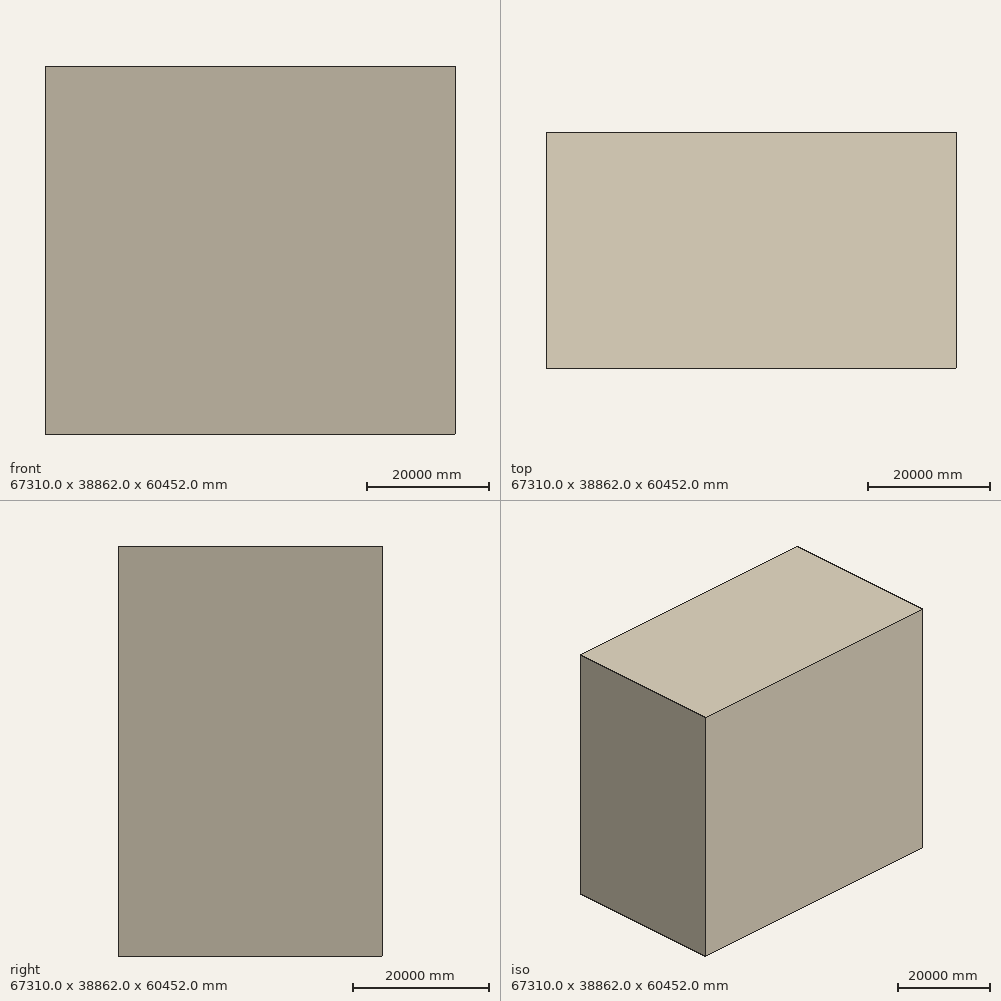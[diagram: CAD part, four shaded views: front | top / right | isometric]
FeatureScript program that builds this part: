
annotation { "Feature Type Name" : "Feature", "Feature Type Description" : "" }
export const myFeature = defineFeature(function(context is Context, id is Id, definition is map)
    precondition{}
    {
        {
            var Q0;
            Q0=qCreatedBy(makeId("Front.planeOp"),FACE);
            var sketch = newSketch(context, id + "F0", { "sketchPlane" : qUnion([Q0])});
            skLineSegment(sketch, "E0.bottom", {"start": v(33655, 30226) * mm, "end": v(-33655, 30226) * mm});
            skLineSegment(sketch, "E0.top", {"start": v(33655, -30226) * mm, "end": v(-33655, -30226) * mm});
            skLineSegment(sketch, "E0.left", {"start": v(33655, 30226) * mm, "end": v(33655, -30226) * mm});
            skLineSegment(sketch, "E0.right", {"start": v(-33655, 30226) * mm, "end": v(-33655, -30226) * mm});
            skPoint(sketch, "E0.middle", {"position": v(0, 0) * mm});
            skSolve(sketch);
        }
        {
            var Q0;
            Q0 = qSketchRegion(id + "F0", true);
            extrude(context, id + "F1", {"entities" : qUnion([Q0]), "depth" : 19431 * mm});
        }
        {
            var Q0;
            Q0=makeQuery(id+"F1.opExtrude","CAP_FACE",FACE,{"disambiguationData":[OSD([sQuery(id+"F0.wireOp",EDGE,"E0.bottom"),sQuery(id+"F0.wireOp",EDGE,"E0.top"),sQuery(id+"F0.wireOp",EDGE,"E0.left"),sQuery(id+"F0.wireOp",EDGE,"E0.right")])],"isStart":true});
            var sketch = newSketch(context, id + "F2", { "sketchPlane" : qUnion([Q0])});
            skLineSegment(sketch, "E1", {"start": v(20955, -30226) * mm, "end": v(20955, -4064) * mm});
            skLineSegment(sketch, "E2", {"start": v(20955, -4064) * mm, "end": v(6985, -4064) * mm});
            skLineSegment(sketch, "E3", {"start": v(6985, -4064) * mm, "end": v(6985, 17526) * mm});
            skLineSegment(sketch, "E4", {"start": v(6985, 17526) * mm, "end": v(-20955, 17526) * mm});
            skLineSegment(sketch, "E5", {"start": v(-20955, 17526) * mm, "end": v(-20955, -30226) * mm});
            skLineSegment(sketch, "E6", {"start": v(-20955, -30226) * mm, "end": v(20955, -30226) * mm});
            skSolve(sketch);
        }
        {
            var Q0;
            Q0 = qSketchRegion(id + "F2", true);
            extrude(context, id + "F3", {"entities" : qUnion([Q0]), "operationType" : NewBodyOperationType.REMOVE, "oppositeDirection" : true, "depth" : 5715 * mm});
        }
        {
            var Q0;
            Q0=makeQuery(id+"F1.opExtrude","SWEPT_BODY",BODY,{"disambiguationData":[OSD([sQuery(id+"F0.wireOp",EDGE,"E0.bottom"),sQuery(id+"F0.wireOp",EDGE,"E0.top"),sQuery(id+"F0.wireOp",EDGE,"E0.left"),sQuery(id+"F0.wireOp",EDGE,"E0.right")])]});
            var Q1;
            Q1=makeQuery(id+"F1.opExtrude","CAP_FACE",FACE,{"disambiguationData":[OSD([sQuery(id+"F0.wireOp",EDGE,"E0.bottom"),sQuery(id+"F0.wireOp",EDGE,"E0.top"),sQuery(id+"F0.wireOp",EDGE,"E0.left"),sQuery(id+"F0.wireOp",EDGE,"E0.right")])],"isStart":true});
            mirror(context, id + "F4", {"operationType" : NewBodyOperationType.ADD, "entities" : qUnion([Q0]), "mirrorPlane" : qUnion([Q1])});
        }
    });
